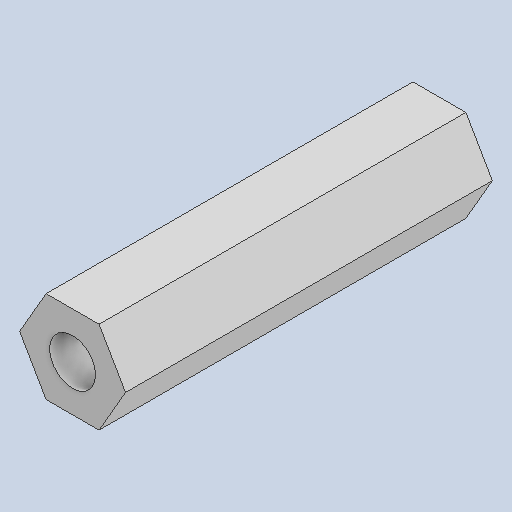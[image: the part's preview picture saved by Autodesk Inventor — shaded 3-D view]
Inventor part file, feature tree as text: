
AUTODESK INVENTOR PART (.ipt)
format: ipt  version: 2024.2 (Build 282272000, 272)  size: 103,936 bytes
history: native  units: mm
features: extrude x2, sketch x1
ambient origin geometry x8: Origin, YZ Plane, XZ Plane, XY Plane, X Axis, Y Axis, Z Axis, Center Point
bodies: Solid1 (feature_tree)
feature tree (3):
  extrude  "Extrusion1"  Depth=20.0mm TaperAngle=0.0deg
  extrude  "Extrusion3"  Depth=20.0mm
  sketch  "Sketch1"  dims[d0=5.0mm d1=20.0mm d2=0.0mm d6=2.5mm d7=7.0mm d8=0.0mm]
